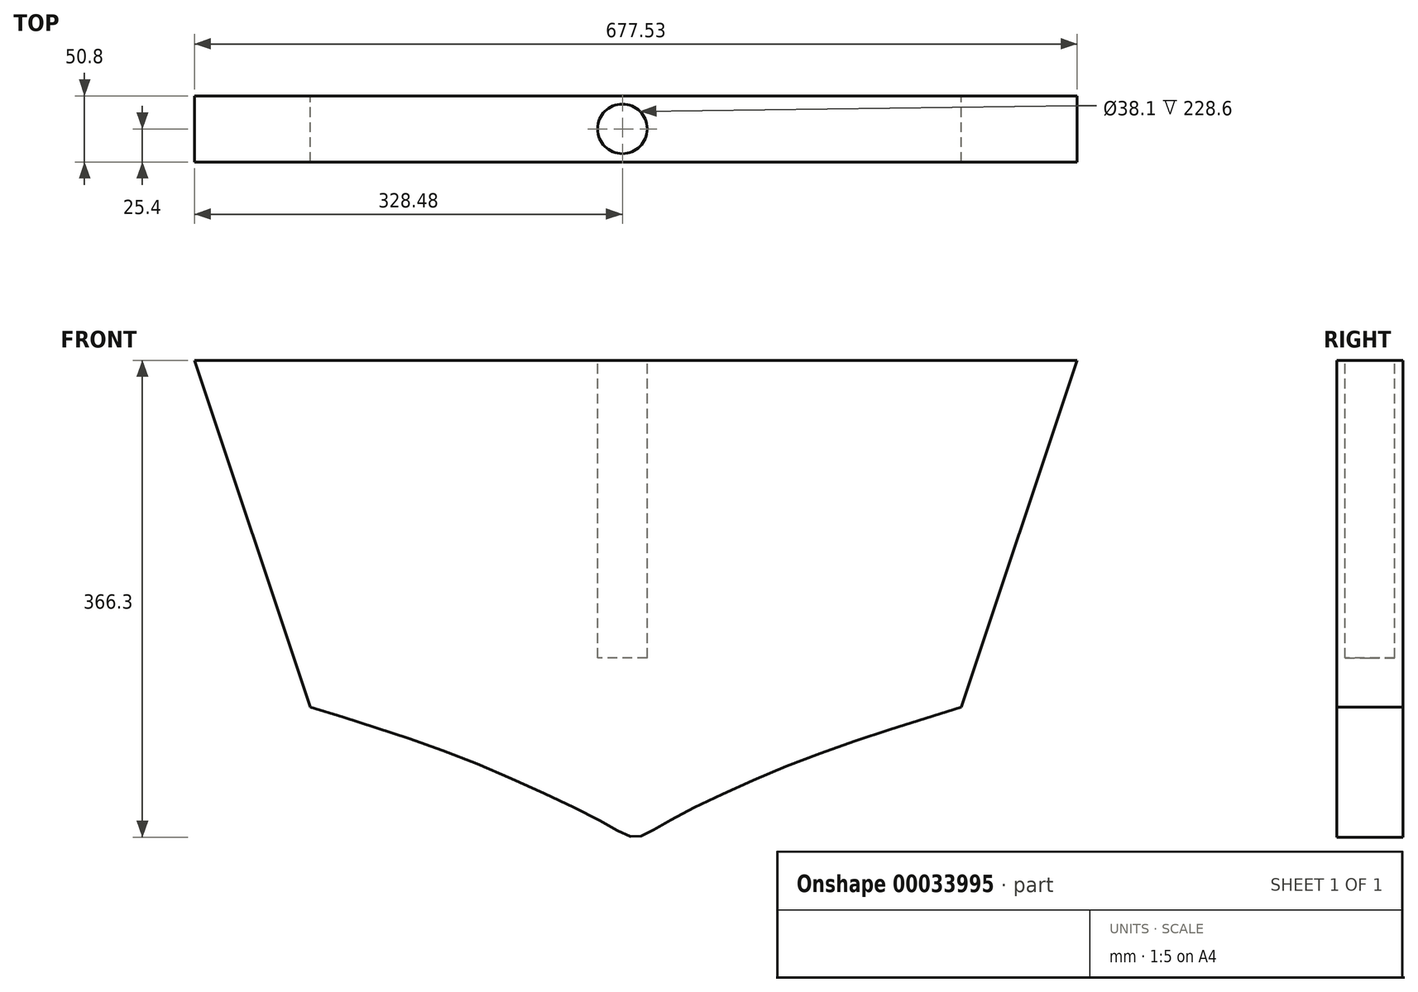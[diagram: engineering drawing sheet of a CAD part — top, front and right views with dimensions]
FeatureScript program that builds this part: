
annotation { "Feature Type Name" : "Feature", "Feature Type Description" : "" }
export const myFeature = defineFeature(function(context is Context, id is Id, definition is map)
    precondition{}
    {
        {
            var Q0;
            Q0=qCreatedBy(makeId("Front.planeOp"),FACE);
            var sketch = newSketch(context, id + "F0", { "sketchPlane" : qUnion([Q0])});
            skLineSegment(sketch, "E0", {"start": v(-328.48, 146.37) * mm, "end": v(349.05, 146.37) * mm});
            skLineSegment(sketch, "E1", {"start": v(349.05, 146.37) * mm, "end": v(260.29, -119.92) * mm});
            skLineSegment(sketch, "E2", {"start": v(-239.71, -119.92) * mm, "end": v(-328.48, 146.37) * mm});
            skPoint(sketch, "E3", {"position": v(0.17, -0.26) * mm});
            skFitSpline(sketch, "E4", {"points": [v(260.29, -119.92) * mm, v(120.83, -167.54) * mm, v(30.3, -210.64) * mm, v(10.29, -219.92) * mm, v(-9.79, -211.43) * mm, v(-113.15, -163.1) * mm, v(-239.71, -119.92) * mm], "startDerivative": vector(-630.83, -196.48) * mm, "endDerivative": vector(-579.14, 178.53) * mm});
            skSolve(sketch);
        }
        {
            var Q0;
            Q0=makeQuery(id+"F0.imprint","IMPRINT",FACE,{"disambiguationData":[TD([[makeQuery(id+"F0.imprint","IMPRINT",EDGE,{"derivedFrom":sQuery(id+"F0.wireOp",EDGE,"E0")}),-1.0]])]});
            extrude(context, id + "F1", {"entities" : qUnion([Q0]), "depth" : 50.8 * mm});
        }
        {
            var Q0;
            Q0=makeQuery(id+"F1.opExtrude","SWEPT_FACE",FACE,{"disambiguationData":[OSD([sQuery(id+"F0.wireOp",EDGE,"E0")])]});
            var sketch = newSketch(context, id + "F2", { "sketchPlane" : qUnion([Q0])});
            skPoint(sketch, "E5", {"position": v(0, -25.4) * mm});
            skCircle(sketch, "E6", {"center": v(0, -25.4) * mm, "radius": 19.05 * mm});
            skSolve(sketch);
        }
        {
            var Q0;
            Q0=makeQuery(id+"F2.imprint","IMPRINT",FACE,{"disambiguationData":[TD([[makeQuery(id+"F2.imprint","IMPRINT",EDGE,{"derivedFrom":sQuery(id+"F2.wireOp",EDGE,"E6")}),1.0]])]});
            extrude(context, id + "F3", {"entities" : qUnion([Q0]), "operationType" : NewBodyOperationType.REMOVE, "oppositeDirection" : true, "depth" : 228.6 * mm});
        }
    });
